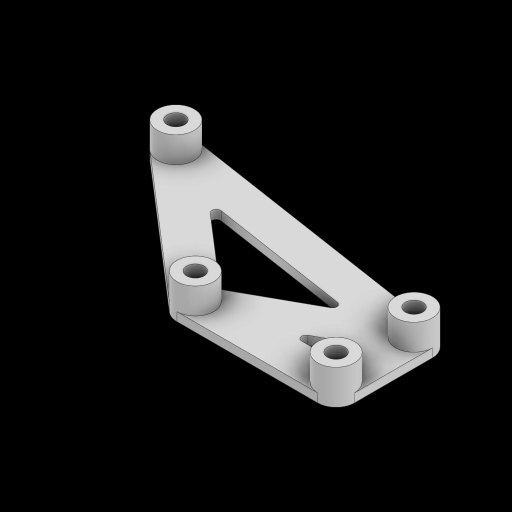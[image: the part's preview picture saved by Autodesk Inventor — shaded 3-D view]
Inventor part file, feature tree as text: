
AUTODESK INVENTOR PART (.ipt)
format: ipt  version: 2024 (Build 280153000, 153)  size: 199,168 bytes
history: native  units: mm
features: projected_geometry x4, extrude x2, sketch x2, fillet x1
ambient origin geometry x8: Origin, YZ Plane, XZ Plane, XY Plane, X Axis, Y Axis, Z Axis, Center Point
bodies: Volumenkörper1 (feature_tree)
feature tree (9):
  extrude  "Extrusion1"  Depth=8.5mm
  extrude  "Extrusion2"  Depth=8.5mm
  fillet  "Rundung1"  Radius=5.0mm
  sketch  "Skizze1"  dims[d0=8.5mm d1=33.0mm]
  sketch  "Skizze2"  dims[d2=5.0mm d3=8.5mm d4=5.0mm d5=37.5mm d6=8.5mm d7=70.0mm d8=23.0mm d9=8.5mm d10=70.0mm d11=5.0mm d12=4.0mm d13=4.0mm d14=4.0mm d15=4.0mm d16=8.0mm d17=0.0mm d18=2.0mm d19=0.0mm d20=1.0mm]
  projected_geometry  "Projizierte Kontur1"
  projected_geometry  "Projizierte Kontur2"
  projected_geometry  "Projizierte Kontur3"
  projected_geometry  "Projizierte Kontur4"
